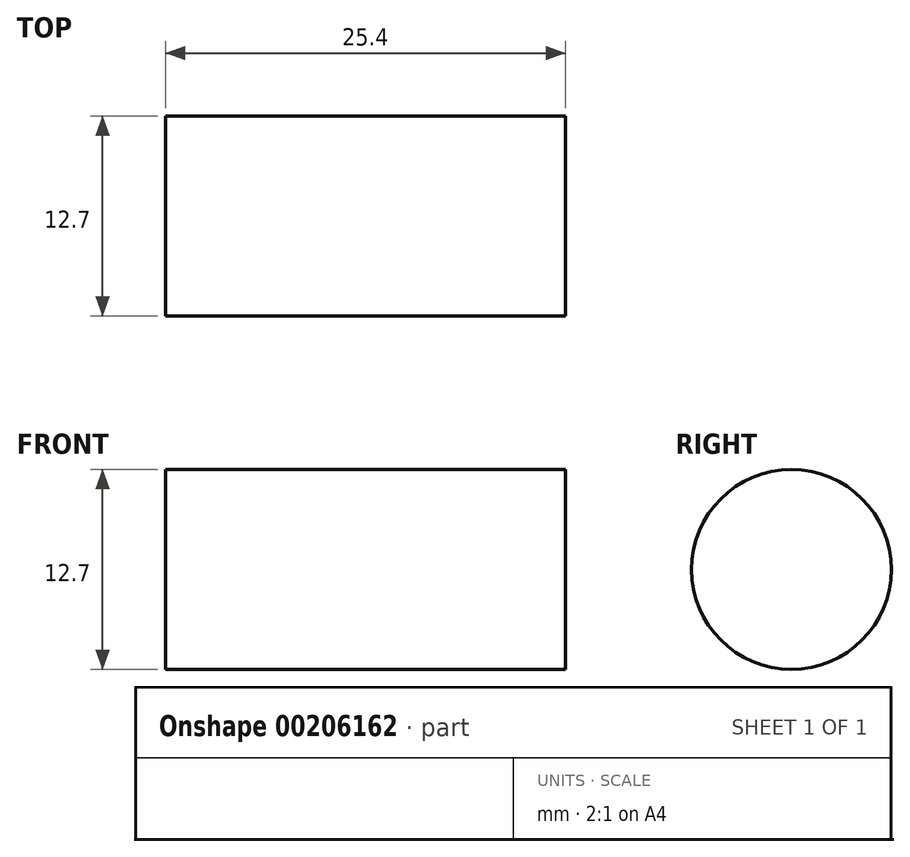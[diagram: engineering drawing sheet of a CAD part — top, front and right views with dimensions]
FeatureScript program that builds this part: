
annotation { "Feature Type Name" : "Feature", "Feature Type Description" : "" }
export const myFeature = defineFeature(function(context is Context, id is Id, definition is map)
    precondition{}
    {
        {
            var Q0;
            Q0=qCreatedBy(makeId("Right.planeOp"),FACE);
            var sketch = newSketch(context, id + "F0", { "sketchPlane" : qUnion([Q0])});
            skCircle(sketch, "E0", {"center": v(0, 0) * mm, "radius": 6.35 * mm});
            skSolve(sketch);
        }
        {
            var Q0;
            Q0 = qSketchRegion(id + "F0", true);
            extrude(context, id + "F1", {"entities" : qUnion([Q0]), "depth" : 25.4 * mm});
        }
    });
